# Revit family: РКВ_І 630_1100_Eng
name_source: partatom
category: Duct Accessories
units: mm (PartAtom-declared; Revit-internal decimal feet)

## family parameters
Always vertical = Yes
Cut with Voids When Loaded = No
Part Type = Attaches To
Round Connector Dimension = Use Diameter
Shared = No
Work Plane-Based = No

## types (12) — shared parameters
00_20_Manufacturer = Vents
00_20_Name = Mounting frame
Casing Material = Metal, painted, blue, matte RAL 5007
Load Classification = HVAC
Maintenance zone material = <By Category>
Manufacturer = Vents
URL = https://ventilation-system.com
zero-valued in all types: Default Elevation

## per-type parameters (varying)
| type | 00_20_Type | B | B1 | B2 | Chamfer | Description | H | Height | L | L1 | L2 | Length | Ln | Weight | Width |
| RKV 630 | RKV 630 | 1212 mm  [stored 3.97638 ft] | 852 mm  [stored 2.79528 ft] | 413 mm  [stored 1.35499 ft] | 229 mm |  | 600 mm | 600 mm | 912 mm  [stored 2.99213 ft] | 750 mm  [stored 2.46063 ft] | 459 mm | 1212 mm  [stored 3.97638 ft] | 917 mm  [stored 3.00853 ft] | 65.90 kg | 1212 mm  [stored 3.97638 ft] |
| RKV 710 | RKV 710 | 1262 mm  [stored 4.14042 ft] | 902 mm  [stored 2.95932 ft] | 438 mm | 242 mm |  | 600 mm | 600 mm | 962 mm  [stored 3.15617 ft] | 840 mm  [stored 2.75591 ft] | 484 mm | 1262 mm  [stored 4.14042 ft] | 967 mm  [stored 3.17257 ft] | 68.50 kg | 1262 mm  [stored 4.14042 ft] |
| RKV 900 | RKV 900 | 1512 mm  [stored 4.96063 ft] | 1152 mm  [stored 3.77953 ft] | 563 mm | 304 mm |  | 650 mm  [stored 2.13255 ft] | 650 mm  [stored 2.13255 ft] | 1212 mm  [stored 3.97638 ft] | 1050 mm  [stored 3.44488 ft] | 609 mm | 1512 mm  [stored 4.96063 ft] | 1217 mm  [stored 3.99278 ft] | 85.70 kg | 1512 mm  [stored 4.96063 ft] |
| RKV 1000 | RKV 1000 | 1712 mm  [stored 5.6168 ft] | 1352 mm  [stored 4.4357 ft] | 663 mm  [stored 2.1752 ft] | 354 mm |  | 730 mm  [stored 2.39501 ft] | 730 mm  [stored 2.39501 ft] | 1412 mm  [stored 4.63255 ft] | 1240 mm  [stored 4.06824 ft] | 709 mm | 1712 mm  [stored 5.6168 ft] | 1417 mm  [stored 4.64895 ft] | 103.70 kg | 1712 mm  [stored 5.6168 ft] |
| RKV 1100 | RKV 1100 | 1712 mm  [stored 5.6168 ft] | 1352 mm  [stored 4.4357 ft] | 663 mm  [stored 2.1752 ft] | 354 mm |  | 730 mm  [stored 2.39501 ft] | 730 mm  [stored 2.39501 ft] | 1412 mm  [stored 4.63255 ft] | 1240 mm  [stored 4.06824 ft] | 709 mm | 1712 mm  [stored 5.6168 ft] | 1417 mm  [stored 4.64895 ft] | 103.70 kg | 1712 mm  [stored 5.6168 ft] |
| RKV 800 | RKV 800 | 1262 mm  [stored 4.14042 ft] | 902 mm  [stored 2.95932 ft] | 438 mm | 242 mm |  | 600 mm | 600 mm | 962 mm  [stored 3.15617 ft] | 840 mm  [stored 2.75591 ft] | 484 mm | 1262 mm  [stored 4.14042 ft] | 967 mm  [stored 3.17257 ft] | 68.50 kg | 1262 mm  [stored 4.14042 ft] |
| RKVI 1000 | RKVI 1000 | 1712 mm  [stored 5.6168 ft] | 1350 mm  [stored 4.42913 ft] | 663 mm  [stored 2.1752 ft] | 354 mm | Isolated | 730 mm  [stored 2.39501 ft] | 730 mm  [stored 2.39501 ft] | 1412 mm  [stored 4.63255 ft] | 1240 mm  [stored 4.06824 ft] | 709 mm | 1712 mm  [stored 5.6168 ft] | 1417 mm  [stored 4.64895 ft] | 140.60 kg | 1712 mm  [stored 5.6168 ft] |
| RKVI 1100 | RKVI 1100 | 1712 mm  [stored 5.6168 ft] | 1350 mm  [stored 4.42913 ft] | 663 mm  [stored 2.1752 ft] | 354 mm | Isolated | 730 mm  [stored 2.39501 ft] | 730 mm  [stored 2.39501 ft] | 1412 mm  [stored 4.63255 ft] | 1240 mm  [stored 4.06824 ft] | 709 mm | 1712 mm  [stored 5.6168 ft] | 1417 mm  [stored 4.64895 ft] | 140.60 kg | 1712 mm  [stored 5.6168 ft] |
| RKVI 630 | RKVI 630 | 1212 mm  [stored 3.97638 ft] | 850 mm  [stored 2.78871 ft] | 413 mm  [stored 1.35499 ft] | 229 mm | Isolated | 600 mm | 600 mm | 912 mm  [stored 2.99213 ft] | 750 mm  [stored 2.46063 ft] | 459 mm | 1212 mm  [stored 3.97638 ft] | 917 mm  [stored 3.00853 ft] | 85.50 kg | 1212 mm  [stored 3.97638 ft] |
| RKVI 710 | RKVI 710 | 1262 mm  [stored 4.14042 ft] | 900 mm  [stored 2.95276 ft] | 438 mm | 242 mm | Isolated | 600 mm | 600 mm | 962 mm  [stored 3.15617 ft] | 840 mm  [stored 2.75591 ft] | 484 mm | 1262 mm  [stored 4.14042 ft] | 967 mm  [stored 3.17257 ft] | 89.00 kg | 1262 mm  [stored 4.14042 ft] |
| RKVI 800 | RKVI 800 | 1262 mm  [stored 4.14042 ft] | 900 mm  [stored 2.95276 ft] | 438 mm | 242 mm | Isolated | 600 mm | 600 mm | 962 mm  [stored 3.15617 ft] | 840 mm  [stored 2.75591 ft] | 484 mm | 1262 mm  [stored 4.14042 ft] | 967 mm  [stored 3.17257 ft] | 89.00 kg | 1262 mm  [stored 4.14042 ft] |
| RKVI 900 | РКВІ 900 | 1512 mm  [stored 4.96063 ft] | 1150 mm | 563 mm | 304 mm | Isolated | 650 mm  [stored 2.13255 ft] | 650 mm  [stored 2.13255 ft] | 1212 mm  [stored 3.97638 ft] | 1050 mm  [stored 3.44488 ft] | 609 mm | 1512 mm  [stored 4.96063 ft] | 1217 mm  [stored 3.99278 ft] | 113.00 kg | 1512 mm  [stored 4.96063 ft] |

note: [stored X ft] marks values corroborated as IEEE doubles in the binary element streams (Revit-internal decimal feet)
